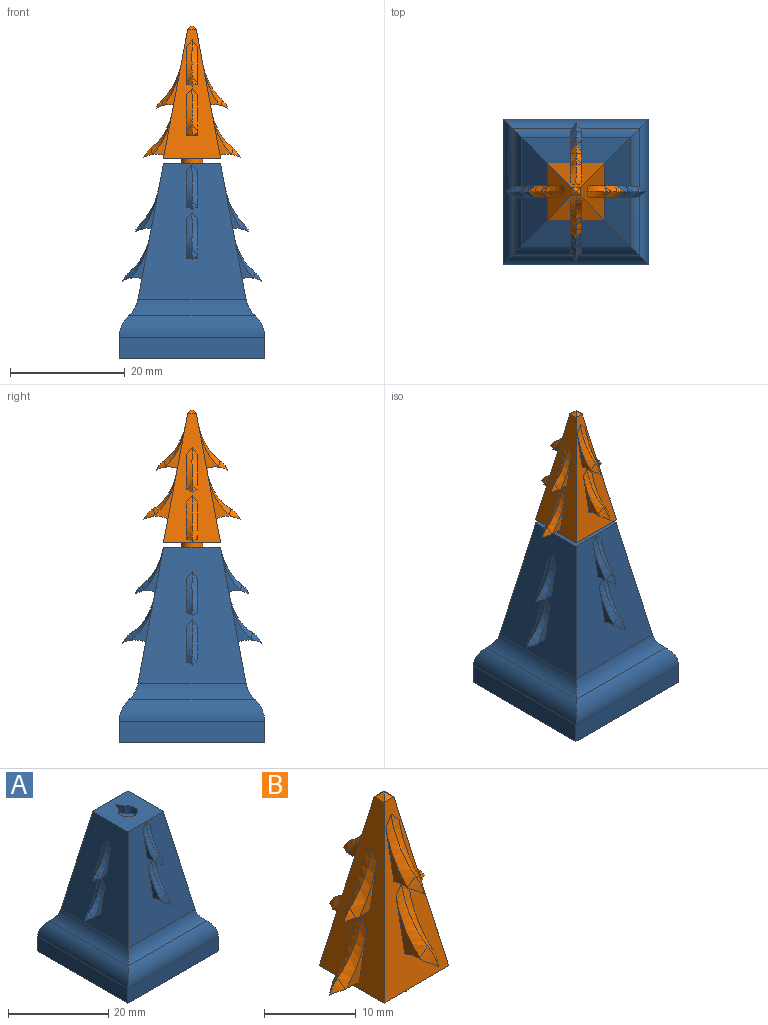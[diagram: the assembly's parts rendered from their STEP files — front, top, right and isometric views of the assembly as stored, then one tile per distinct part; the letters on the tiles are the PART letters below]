
ASSEMBLY  parts=2 mates=1
PART A: 78 faces, bbox 26.3x26.3x36.3 mm
  f0: plane 9.94x9.94mm, normal (0,0,1), area 86.1mm2, adj f1,f2,f3,f4,f74,f75,f76
  f1: plane 23.85x18.88mm, normal (0,-0.98,0.18), area 319.5mm2, adj f0,f3,f4,f16,f17,f18,f19,f20
  f2: plane 23.85x18.88mm, normal (0,0.98,0.18), area 319.5mm2, adj f0,f3,f4,f10,f11,f12,f13,f14
  f3: plane 23.85x18.88mm, normal (-0.98,0,0.18), area 321.5mm2, adj f0,f1,f2,f36,f37,f38,f39,f40
  f4: plane 23.85x18.88mm, normal (0.98,0,0.18), area 321.5mm2, adj f0,f1,f2,f30,f31,f32,f33,f34
  f5: plane 25.4x3.59mm, normal (1,0,0), area 91.1mm2, adj f6,f8,f9,f70
  f6: plane 25.4x3.59mm, normal (0,1,0), area 91.1mm2, adj f5,f7,f9,f71
  f7: plane 25.4x3.59mm, normal (-1,0,0), area 91.1mm2, adj f6,f8,f9,f73
  f8: plane 25.4x3.59mm, normal (0,-1,0), area 91.1mm2, adj f5,f7,f9,f72
  f9: plane 25.4x25.4mm, normal (0,0,-1), area 645.2mm2, adj f5,f6,f7,f8
  f10: cylinder r=4.43mm len=3.51mm, axis (1,0,0), area 5.7mm2, adj f2,f11,f12,f24,f25,f58,f59
  f11: plane 6.49x3.21mm, normal (-1,0,0), area 4mm2, adj f2,f10,f59
  f12: plane 6.49x3.21mm, normal (1,0,0), area 4mm2, adj f2,f10,f58
  f13: cylinder r=4.43mm len=4.06mm, axis (1,0,0), area 6.9mm2, adj f2,f14,f15,f22,f23
  f14: plane 7.84x4.74mm, normal (-1,0,0), area 5.2mm2, adj f2,f13,f22,f61
  f15: plane 7.85x4.75mm, normal (1,0,0), area 5.2mm2, adj f2,f13,f23,f60
  f16: cylinder r=4.43mm len=3.51mm, axis (1,0,0), area 5.7mm2, adj f1,f17,f18,f28,f29,f54,f55
  f17: plane 6.49x3.21mm, normal (-1,0,0), area 4mm2, adj f1,f16,f55
  f18: plane 6.49x3.21mm, normal (1,0,0), area 4mm2, adj f1,f16,f54
  f19: cylinder r=4.43mm len=4.06mm, axis (1,0,0), area 6.9mm2, adj f1,f20,f21,f26,f27
  f20: plane 7.84x4.75mm, normal (-1,0,0), area 5.2mm2, adj f1,f19,f26,f57
  f21: plane 7.84x4.74mm, normal (1,0,0), area 5.2mm2, adj f1,f19,f27,f56
  f22: cone r=3.73mm half-angle=45deg, axis (1,0,0), area 1.9mm2, adj f13,f14,f23,f61
  f23: cone r=2.71mm half-angle=45deg, axis (-1,0,0), area 1.9mm2, adj f13,f15,f22,f60
  f24: cone r=3.73mm half-angle=45deg, axis (1,0,0), area 1.3mm2, adj f10,f25,f59
  f25: cone r=2.71mm half-angle=45deg, axis (-1,0,0), area 1.3mm2, adj f10,f24,f58
  f26: cone r=2.71mm half-angle=45deg, axis (1,0,0), area 1.9mm2, adj f19,f20,f27,f57
  f27: cone r=3.73mm half-angle=45deg, axis (-1,0,0), area 1.9mm2, adj f19,f21,f26,f56
  f28: cone r=2.71mm half-angle=45deg, axis (1,0,0), area 1.3mm2, adj f16,f29,f55
  f29: cone r=3.73mm half-angle=45deg, axis (-1,0,0), area 1.3mm2, adj f16,f28,f54
  f30: cylinder r=4.43mm len=2.83mm, axis (0,1,0), area 4.4mm2, adj f4,f31,f32,f46,f47,f52,f53
  f31: plane 6x2.54mm, normal (0,-1,0), area 2.8mm2, adj f4,f30,f53
  f32: plane 6x2.54mm, normal (0,1,0), area 2.8mm2, adj f4,f30,f52
  f33: cylinder r=4.43mm len=3.39mm, axis (0,1,0), area 5.5mm2, adj f4,f34,f35,f48,f49,f50,f51
  f34: plane 6.39x3.07mm, normal (0,-1,0), area 3.8mm2, adj f4,f33,f51
  f35: plane 6.39x3.07mm, normal (0,1,0), area 3.8mm2, adj f4,f33,f50
  f36: cylinder r=4.43mm len=2.83mm, axis (0,1,0), area 4.4mm2, adj f3,f37,f38,f44,f45,f62,f63
  f37: plane 6x2.54mm, normal (0,-1,0), area 2.8mm2, adj f3,f36,f63
  f38: plane 6x2.54mm, normal (0,1,0), area 2.8mm2, adj f3,f36,f62
  f39: cylinder r=4.43mm len=3.39mm, axis (0,1,0), area 5.5mm2, adj f3,f40,f41,f42,f43,f64,f65
  f40: plane 6.39x3.07mm, normal (0,-1,0), area 3.8mm2, adj f3,f39,f64
  f41: plane 6.39x3.07mm, normal (0,1,0), area 3.8mm2, adj f3,f39,f65
  f42: cone r=2.71mm half-angle=45deg, axis (0,-1,0), area 1.2mm2, adj f39,f43,f65
  f43: cone r=3.73mm half-angle=45deg, axis (0,1,0), area 1.2mm2, adj f39,f42,f64
  f44: cone r=3.73mm half-angle=45deg, axis (0,1,0), area 0.7mm2, adj f36,f45,f63
  f45: cone r=2.71mm half-angle=45deg, axis (0,-1,0), area 0.7mm2, adj f36,f44,f62
  f46: cone r=2.71mm half-angle=45deg, axis (0,1,0), area 0.7mm2, adj f30,f47,f53
  f47: cone r=3.73mm half-angle=45deg, axis (0,-1,0), area 0.7mm2, adj f30,f46,f52
  f48: cone r=2.71mm half-angle=45deg, axis (0,1,0), area 1.2mm2, adj f33,f49,f51
  f49: cone r=3.73mm half-angle=45deg, axis (0,-1,0), area 1.2mm2, adj f33,f48,f50
  f50: bspline ~9.59x9.16mm, area 8.3mm2, adj f4,f33,f35,f49,f51
  f51: bspline ~9.59x9.16mm, area 8.3mm2, adj f4,f33,f34,f48,f50
  f52: bspline ~9.6x9.46mm, area 8.1mm2, adj f4,f30,f32,f47,f53
  f53: bspline ~9.6x9.46mm, area 8.1mm2, adj f4,f30,f31,f46,f52
  f54: bspline ~9.61x9.14mm, area 8.4mm2, adj f1,f16,f18,f29,f55
  f55: bspline ~9.61x9.14mm, area 8.4mm2, adj f1,f16,f17,f28,f54
  f56: bspline ~9.93x9.35mm, area 9.1mm2, adj f1,f21,f27,f57
  f57: bspline ~9.93x9.35mm, area 9.1mm2, adj f1,f20,f26,f56
  f58: bspline ~9.61x9.14mm, area 8.4mm2, adj f2,f10,f12,f25,f59
  f59: bspline ~9.61x9.14mm, area 8.4mm2, adj f2,f10,f11,f24,f58
  f60: bspline ~9.93x9.35mm, area 9.1mm2, adj f2,f15,f23,f61
  f61: bspline ~9.93x9.35mm, area 9.1mm2, adj f2,f14,f22,f60
  f62: bspline ~9.6x9.46mm, area 8.1mm2, adj f3,f36,f38,f45,f63
  f63: bspline ~9.6x9.46mm, area 8.1mm2, adj f3,f36,f37,f44,f62
  f64: bspline ~9.59x9.16mm, area 8.3mm2, adj f3,f39,f40,f43,f65
  f65: bspline ~9.59x9.16mm, area 8.3mm2, adj f3,f39,f41,f42,f64
  f66: cylinder r=5.08mm len=22.05mm, axis (0,1,0), area 67.6mm2, adj f3,f67,f68,f73
  f67: cylinder r=5.08mm len=22.05mm, axis (1,0,0), area 67.6mm2, adj f1,f66,f69,f72
  f68: cylinder r=5.08mm len=22.05mm, axis (1,0,0), area 67.6mm2, adj f2,f66,f69,f71
  f69: cylinder r=5.08mm len=22.05mm, axis (0,1,0), area 67.6mm2, adj f4,f67,f68,f70
  f70: cylinder r=5.08mm len=25.4mm, axis (0,1,0), area 100.7mm2, adj f5,f69,f71,f72
  f71: cylinder r=5.08mm len=25.4mm, axis (1,0,0), area 100.7mm2, adj f6,f68,f70,f73
  f72: cylinder r=5.08mm len=25.4mm, axis (1,0,0), area 100.7mm2, adj f8,f67,f70,f73
  f73: cylinder r=5.08mm len=25.4mm, axis (0,1,0), area 100.7mm2, adj f7,f66,f71,f72
  f74: plane 1.78x1.76mm, normal (0.9,-0.44,0), area 3.5mm2, adj f0,f75,f76,f77
  f75: cylinder r=1.91mm len=3.81mm, axis (0,0,1), area 18.1mm2, adj f0,f74,f76,f77
  f76: plane 1.78x1.76mm, normal (-0.9,-0.44,0), area 3.5mm2, adj f0,f74,f75,f77
  f77: plane 5.36x3.81mm, normal (0,0,1), area 12.7mm2, adj f74,f75,f76
PART B: 70 faces, bbox 17.8x17.8x25.9 mm
  f0: plane 22.59x9.98mm, normal (0,-0.98,0.18), area 101.3mm2, adj f2,f3,f4,f14,f15,f16,f17,f18
  f1: plane 22.59x9.98mm, normal (0,0.98,0.18), area 101.3mm2, adj f2,f3,f7,f8,f9,f10,f11,f12
  f2: plane 22.59x9.98mm, normal (-0.98,0,0.18), area 103.4mm2, adj f0,f1,f6,f34,f35,f36,f37,f38
  f3: plane 22.59x9.98mm, normal (0.98,0,0.18), area 103.4mm2, adj f0,f1,f5,f28,f29,f30,f31,f32
  f4: plane 1.5x0.75mm, normal (0,-0.64,0.77), area 0.7mm2, adj f0,f5,f6
  f5: plane 1.5x0.75mm, normal (0.64,0,0.77), area 0.7mm2, adj f3,f4,f7
  f6: plane 1.5x0.75mm, normal (-0.64,0,0.77), area 0.7mm2, adj f2,f4,f7
  f7: plane 1.5x0.75mm, normal (0,0.64,0.77), area 0.7mm2, adj f1,f5,f6
  f8: cylinder r=4.43mm len=3.68mm, axis (1,0,0), area 6.1mm2, adj f1,f9,f10,f20,f21
  f9: plane 7.55x4.33mm, normal (-1,0,0), area 4.4mm2, adj f1,f8,f20,f59
  f10: plane 7.53x4.3mm, normal (1,0,0), area 4.4mm2, adj f1,f8,f21,f58
  f11: cylinder r=4.43mm len=4.22mm, axis (1,0,0), area 7.3mm2, adj f1,f12,f13,f22,f23
  f12: plane 7.99x4.94mm, normal (-1,0,0), area 5.6mm2, adj f1,f11,f22,f57
  f13: plane 7.99x4.94mm, normal (1,0,0), area 5.6mm2, adj f1,f11,f23,f56
  f14: cylinder r=4.43mm len=3.68mm, axis (1,0,0), area 6.1mm2, adj f0,f15,f16,f26,f27
  f15: plane 7.53x4.3mm, normal (-1,0,0), area 4.4mm2, adj f0,f14,f26,f55
  f16: plane 7.55x4.33mm, normal (1,0,0), area 4.4mm2, adj f0,f14,f27,f54
  f17: cylinder r=4.43mm len=4.22mm, axis (1,0,0), area 7.3mm2, adj f0,f18,f19,f24,f25
  f18: plane 7.99x4.94mm, normal (-1,0,0), area 5.6mm2, adj f0,f17,f24,f49
  f19: plane 7.99x4.94mm, normal (1,0,0), area 5.6mm2, adj f0,f17,f25,f48
  f20: cone r=3.73mm half-angle=45deg, axis (1,0,0), area 1.6mm2, adj f8,f9,f21,f59
  f21: cone r=2.71mm half-angle=45deg, axis (-1,0,0), area 1.6mm2, adj f8,f10,f20,f58
  f22: cone r=3.73mm half-angle=45deg, axis (1,0,0), area 2.1mm2, adj f11,f12,f23,f57
  f23: cone r=2.71mm half-angle=45deg, axis (-1,0,0), area 2.1mm2, adj f11,f13,f22,f56
  f24: cone r=2.71mm half-angle=45deg, axis (1,0,0), area 2.1mm2, adj f17,f18,f25,f49
  f25: cone r=3.73mm half-angle=45deg, axis (-1,0,0), area 2.1mm2, adj f17,f19,f24,f48
  f26: cone r=2.71mm half-angle=45deg, axis (1,0,0), area 1.6mm2, adj f14,f15,f27,f55
  f27: cone r=3.73mm half-angle=45deg, axis (-1,0,0), area 1.6mm2, adj f14,f16,f26,f54
  f28: cylinder r=4.43mm len=3mm, axis (0,1,0), area 4.7mm2, adj f3,f29,f30,f44,f45,f52,f53
  f29: plane 6.1x2.69mm, normal (0,-1,0), area 3.1mm2, adj f3,f28,f53
  f30: plane 6.1x2.69mm, normal (0,1,0), area 3.1mm2, adj f3,f28,f52
  f31: cylinder r=4.43mm len=3.55mm, axis (0,1,0), area 5.8mm2, adj f3,f32,f33,f46,f47,f50,f51
  f32: plane 6.52x3.25mm, normal (0,-1,0), area 4.1mm2, adj f3,f31,f51
  f33: plane 6.52x3.25mm, normal (0,1,0), area 4.1mm2, adj f3,f31,f50
  f34: cylinder r=4.43mm len=3mm, axis (0,1,0), area 4.7mm2, adj f2,f35,f36,f42,f43,f60,f61
  f35: plane 6.1x2.69mm, normal (0,-1,0), area 3.1mm2, adj f2,f34,f61
  f36: plane 6.1x2.69mm, normal (0,1,0), area 3.1mm2, adj f2,f34,f60
  f37: cylinder r=4.43mm len=3.55mm, axis (0,1,0), area 5.8mm2, adj f2,f38,f39,f40,f41,f62,f63
  f38: plane 6.52x3.25mm, normal (0,-1,0), area 4.1mm2, adj f2,f37,f62
  f39: plane 6.52x3.25mm, normal (0,1,0), area 4.1mm2, adj f2,f37,f63
  f40: cone r=2.71mm half-angle=45deg, axis (0,-1,0), area 1.4mm2, adj f37,f41,f63
  f41: cone r=3.73mm half-angle=45deg, axis (0,1,0), area 1.4mm2, adj f37,f40,f62
  f42: cone r=3.73mm half-angle=45deg, axis (0,1,0), area 0.8mm2, adj f34,f43,f61
  f43: cone r=2.71mm half-angle=45deg, axis (0,-1,0), area 0.8mm2, adj f34,f42,f60
  f44: cone r=2.71mm half-angle=45deg, axis (0,1,0), area 0.8mm2, adj f28,f45,f53
  f45: cone r=3.73mm half-angle=45deg, axis (0,-1,0), area 0.8mm2, adj f28,f44,f52
  f46: cone r=2.71mm half-angle=45deg, axis (0,1,0), area 1.4mm2, adj f31,f47,f51
  f47: cone r=3.73mm half-angle=45deg, axis (0,-1,0), area 1.4mm2, adj f31,f46,f50
  f48: bspline ~9.85x9.23mm, area 9.1mm2, adj f0,f19,f25,f49
  f49: bspline ~9.85x9.23mm, area 9.1mm2, adj f0,f18,f24,f48
  f50: bspline ~9.62x9.14mm, area 8.4mm2, adj f3,f31,f33,f47,f51
  f51: bspline ~9.62x9.14mm, area 8.4mm2, adj f3,f31,f32,f46,f50
  f52: bspline ~9.53x9.24mm, area 8.2mm2, adj f3,f28,f30,f45,f53
  f53: bspline ~9.53x9.24mm, area 8.2mm2, adj f3,f28,f29,f44,f52
  f54: bspline ~9.64x9.12mm, area 9mm2, adj f0,f16,f27,f55
  f55: bspline ~9.64x9.12mm, area 9mm2, adj f0,f15,f26,f54
  f56: bspline ~9.85x9.23mm, area 9.1mm2, adj f1,f13,f23,f57
  f57: bspline ~9.85x9.23mm, area 9.1mm2, adj f1,f12,f22,f56
  f58: bspline ~9.64x9.12mm, area 9mm2, adj f1,f10,f21,f59
  f59: bspline ~9.64x9.12mm, area 9mm2, adj f1,f9,f20,f58
  f60: bspline ~9.53x9.24mm, area 8.2mm2, adj f2,f34,f36,f43,f61
  f61: bspline ~9.53x9.24mm, area 8.2mm2, adj f2,f34,f35,f42,f60
  f62: bspline ~9.62x9.14mm, area 8.4mm2, adj f2,f37,f38,f41,f63
  f63: bspline ~9.62x9.14mm, area 8.4mm2, adj f2,f37,f39,f40,f62
  f64: plane 9.98x9.98mm, normal (0,0,-1), area 88.1mm2, adj f0,f1,f2,f3,f65
  f65: cylinder r=1.91mm len=3.81mm, axis (0,0,1), area 20.4mm2, adj f64,f66,f67,f68,f69
  f66: plane 1.76x1.72mm, normal (0,0,1), area 1.3mm2, adj f65,f67,f68
  f67: plane 1.76x0.86mm, normal (0.9,-0.44,0), area 1mm2, adj f65,f66,f68,f69
  f68: plane 1.76x0.86mm, normal (-0.9,-0.44,0), area 1mm2, adj f65,f66,f67,f69
  f69: plane 5.36x3.81mm, normal (0,0,-1), area 12.7mm2, adj f65,f67,f68
PLACE A t=(-20.97,15.54,-3.28)mm fixed
PLACE B t=(-20.97,15.54,-2.47)mm
MATE slider A.f75 <-> B.f65  axis (0,0,1) through (-20.97,15.54,28.98)mm
